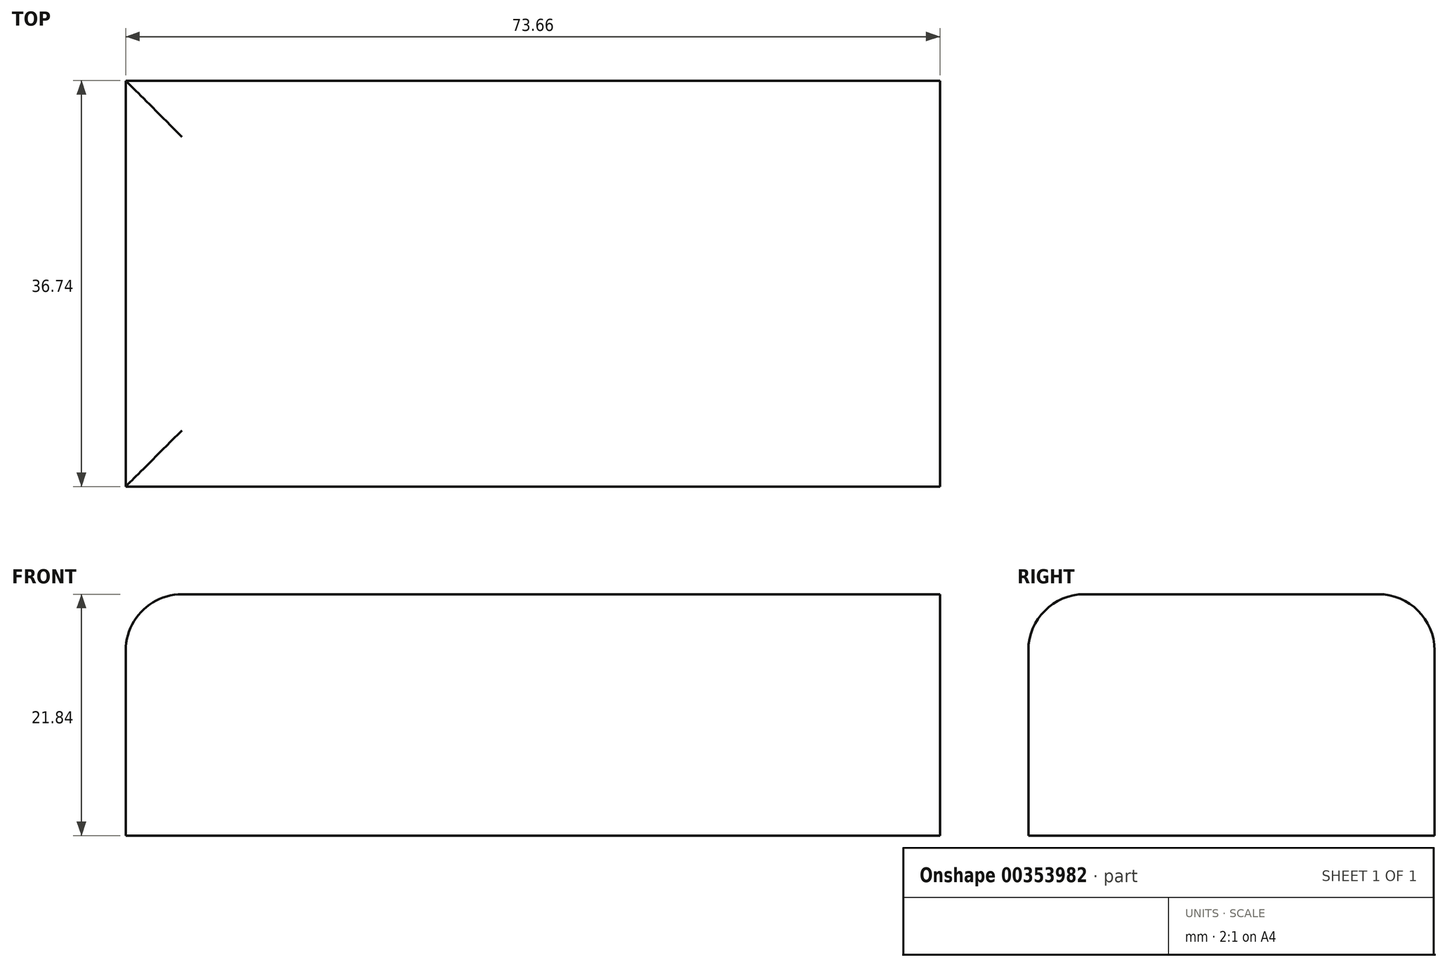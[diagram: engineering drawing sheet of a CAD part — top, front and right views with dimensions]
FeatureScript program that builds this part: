
annotation { "Feature Type Name" : "Feature", "Feature Type Description" : "" }
export const myFeature = defineFeature(function(context is Context, id is Id, definition is map)
    precondition{}
    {
        {
            var Q0;
            Q0=qCreatedBy(makeId("Top.planeOp"),FACE);
            var sketch = newSketch(context, id + "F0", { "sketchPlane" : qUnion([Q0])});
            skLineSegment(sketch, "E0.bottom", {"start": v(-36.83, -18.37) * mm, "end": v(36.83, -18.37) * mm});
            skLineSegment(sketch, "E0.top", {"start": v(-36.83, 18.37) * mm, "end": v(36.83, 18.37) * mm});
            skLineSegment(sketch, "E0.left", {"start": v(-36.83, -18.37) * mm, "end": v(-36.83, 18.37) * mm});
            skLineSegment(sketch, "E0.right", {"start": v(36.83, -18.37) * mm, "end": v(36.83, 18.37) * mm});
            skPoint(sketch, "E0.middle", {"position": v(0, 0) * mm});
            skSolve(sketch);
        }
        {
            var Q0;
            Q0 = qSketchRegion(id + "F0", true);
            extrude(context, id + "F1", {"entities" : qUnion([Q0]), "endBound" : BoundingType.SYMMETRIC, "depth" : 21.84 * mm});
        }
        {
            var Q0;
            Q0=makeQuery(id+"F1.opExtrude","CAP_EDGE",EDGE,{"disambiguationData":[OSD([sQuery(id+"F0.wireOp",EDGE,"E0.left")])],"isStart":false});
            var Q1;
            Q1=makeQuery(id+"F1.opExtrude","CAP_EDGE",EDGE,{"disambiguationData":[OSD([sQuery(id+"F0.wireOp",EDGE,"E0.bottom")])],"isStart":false});
            var Q2;
            Q2=makeQuery(id+"F1.opExtrude","CAP_EDGE",EDGE,{"disambiguationData":[OSD([sQuery(id+"F0.wireOp",EDGE,"E0.top")])],"isStart":false});
            fillet(context, id + "F2", {"entities" : qUnion([Q0, Q1, Q2]), "radius" : 5.08 * mm, "tangentPropagation" : true, "allowEdgeOverflow" : false});
        }
    });
